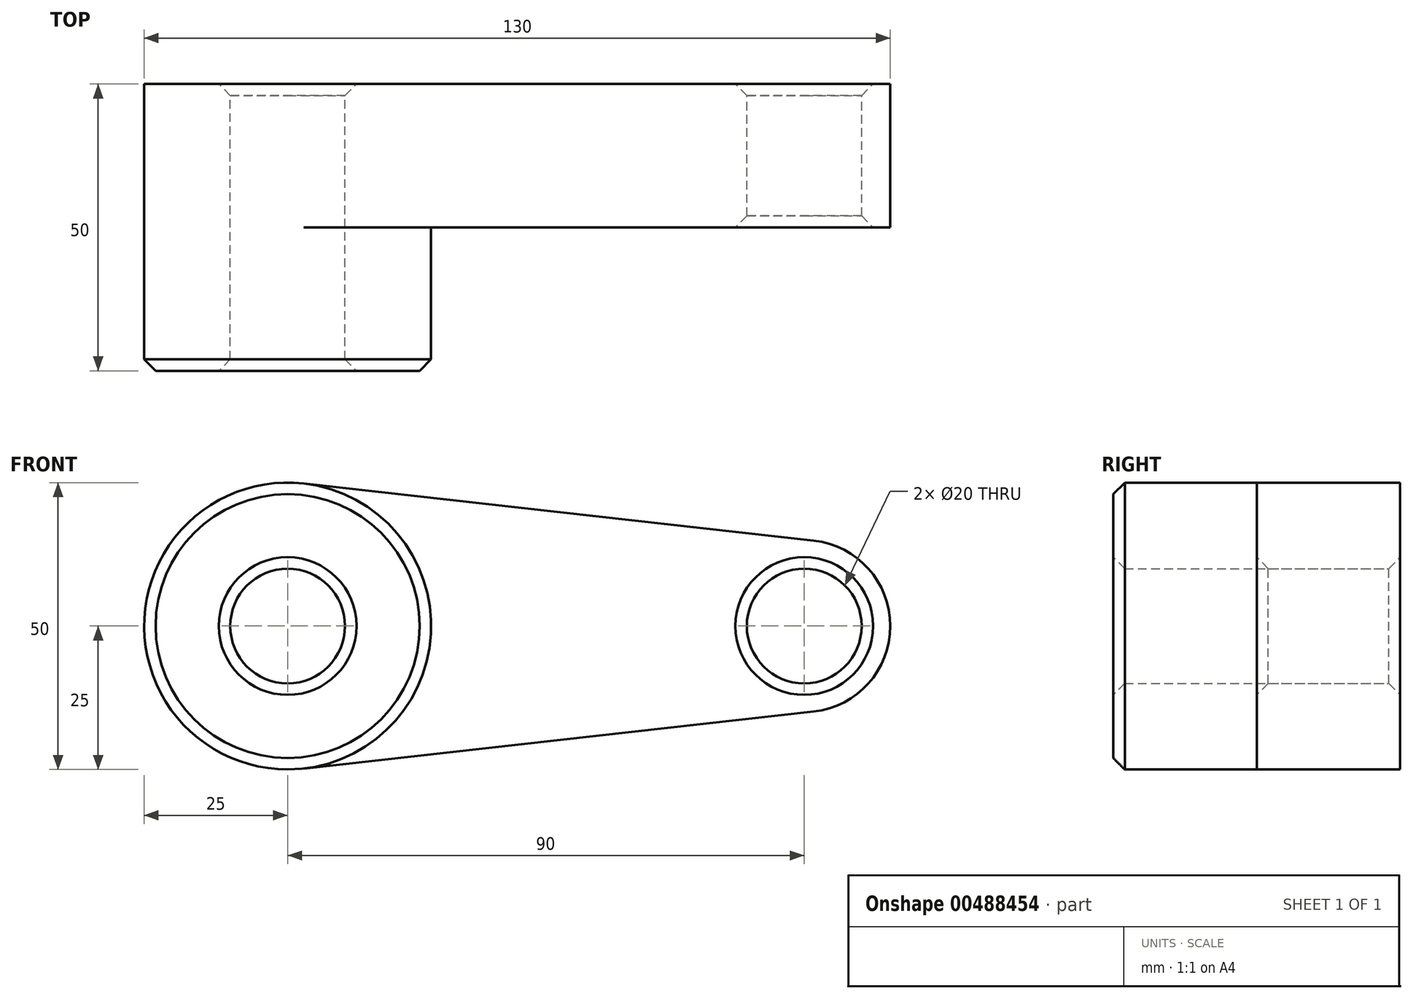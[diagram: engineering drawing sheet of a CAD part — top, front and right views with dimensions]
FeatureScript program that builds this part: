
annotation { "Feature Type Name" : "Feature", "Feature Type Description" : "" }
export const myFeature = defineFeature(function(context is Context, id is Id, definition is map)
    precondition{}
    {
        {
            var Q0;
            Q0=qCreatedBy(makeId("Front.planeOp"),FACE);
            var sketch = newSketch(context, id + "F0", { "sketchPlane" : qUnion([Q0])});
            skCircle(sketch, "E0", {"center": v(0, 0) * mm, "radius": 25 * mm});
            skCircle(sketch, "E1", {"center": v(90, 0) * mm, "radius": 15 * mm});
            skLineSegment(sketch, "E2", {"start": v(2.78, -24.85) * mm, "end": v(91.67, -14.9) * mm});
            skLineSegment(sketch, "E3", {"start": v(2.78, 24.85) * mm, "end": v(91.67, 14.9) * mm});
            skCircle(sketch, "E4", {"center": v(0, 0) * mm, "radius": 10 * mm});
            skCircle(sketch, "E5", {"center": v(90, 0) * mm, "radius": 10 * mm});
            skSolve(sketch);
        }
        {
            var Q0;
            Q0 = qSketchRegion(id + "F0", true);
            extrude(context, id + "F1", {"entities" : qUnion([Q0]), "depth" : 25 * mm});
        }
        {
            var Q0;
            Q0=makeQuery(id+"F0.imprint","IMPRINT",FACE,{"disambiguationData":[TD([[makeQuery(id+"F0.imprint","IMPRINT",EDGE,{"derivedFrom":sQuery(id+"F0.wireOp",EDGE,"E4")}),-1.0]])]});
            extrude(context, id + "F2", {"entities" : qUnion([Q0]), "operationType" : NewBodyOperationType.ADD, "depth" : 50 * mm});
        }
        {
            var Q0;
            Q0=makeQuery(id+"F2.opExtrude","CAP_EDGE",EDGE,{"disambiguationData":[OSD([sQuery(id+"F0.wireOp",EDGE,"E4")])],"isStart":false});
            var Q1;
            Q1=makeQuery(id+"F1.opExtrude","CAP_EDGE",EDGE,{"disambiguationData":[OSD([sQuery(id+"F0.wireOp",EDGE,"E4")])],"isStart":true});
            var Q2;
            Q2=makeQuery(id+"F2.opExtrude","CAP_EDGE",EDGE,{"disambiguationData":[OSD([sQuery(id+"F0.wireOp",EDGE,"E0")])],"isStart":false});
            var Q3;
            Q3=makeQuery(id+"F1.opExtrude","CAP_EDGE",EDGE,{"disambiguationData":[OSD([sQuery(id+"F0.wireOp",EDGE,"E5")])],"isStart":true});
            var Q4;
            Q4=makeQuery(id+"F1.opExtrude","CAP_EDGE",EDGE,{"disambiguationData":[OSD([sQuery(id+"F0.wireOp",EDGE,"E5")])],"isStart":false});
            chamfer(context, id + "F3", {"entities" : qUnion([Q0, Q1, Q2, Q3, Q4]), "width" : 2 * mm, "tangentPropagation" : true});
        }
    });
